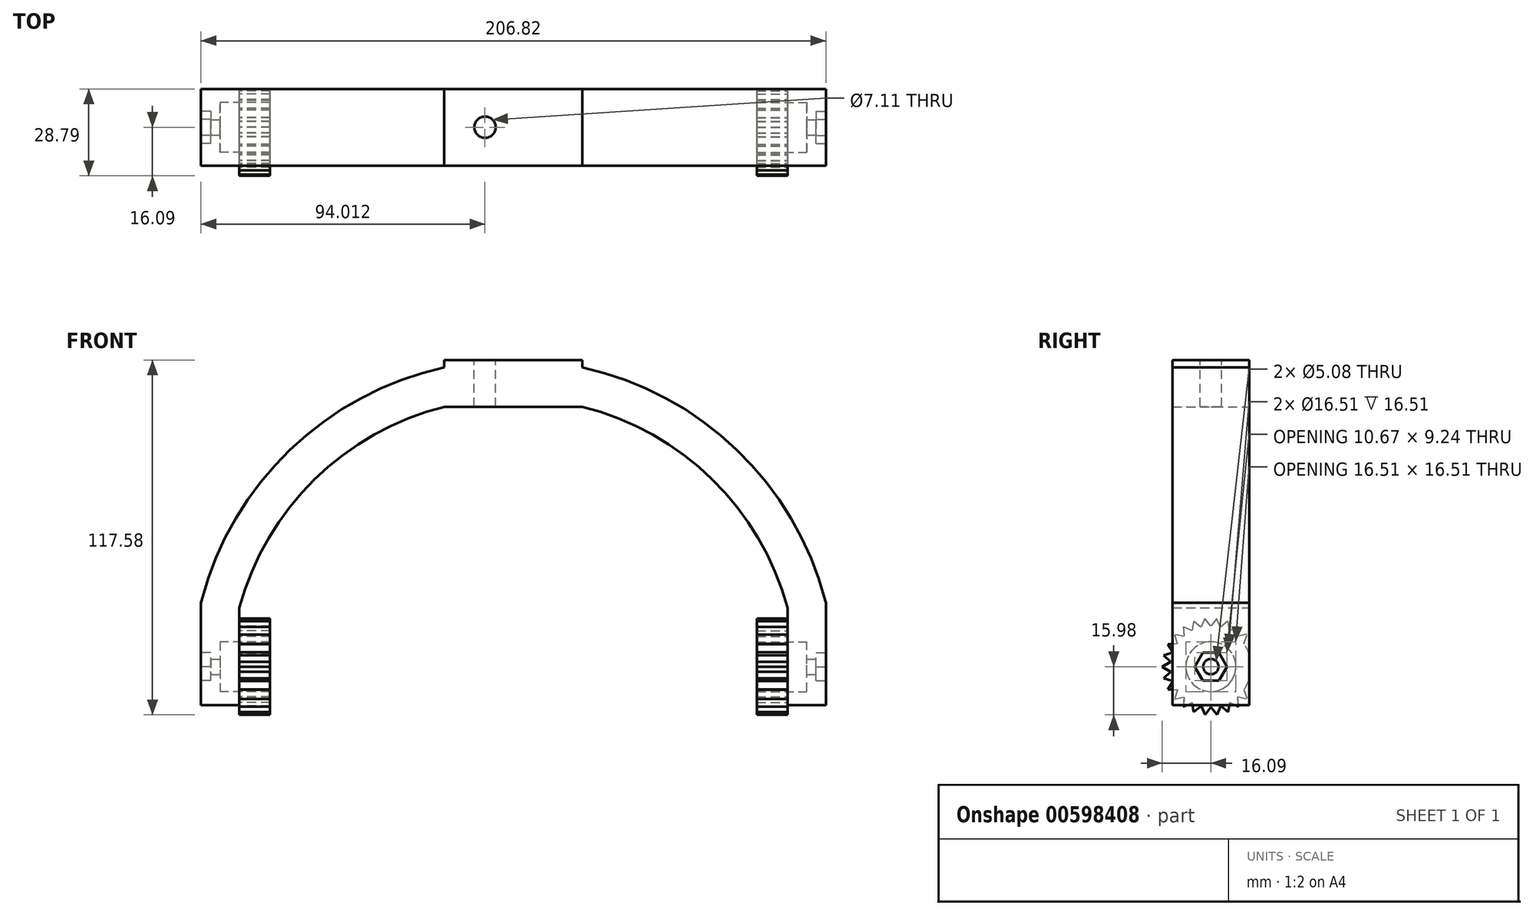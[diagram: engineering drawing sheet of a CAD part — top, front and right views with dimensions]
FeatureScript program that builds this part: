
annotation { "Feature Type Name" : "Feature", "Feature Type Description" : "" }
export const myFeature = defineFeature(function(context is Context, id is Id, definition is map)
    precondition{}
    {
        {
            var Q0;
            Q0=qCreatedBy(makeId("Front.planeOp"),FACE);
            var sketch = newSketch(context, id + "F0", { "sketchPlane" : qUnion([Q0])});
            skArc(sketch, "E0", {"start": v(97.06, 33.02) * mm, "mid": v(0, 107.95) * mm, "end": v(-97.06, 33.02) * mm});
            skLineSegment(sketch, "E1", {"start": v(-97.06, 33.02) * mm, "end": v(-97.06, 0) * mm});
            skLineSegment(sketch, "E2", {"start": v(97.06, 33.02) * mm, "end": v(97.06, 0) * mm});
            skSolve(sketch);
        }
        {
            var Q0;
            Q0=qCreatedBy(makeId("Top.planeOp"),FACE);
            var sketch = newSketch(context, id + "F1", { "sketchPlane" : qUnion([Q0])});
            skPoint(sketch, "E3.0", {"position": v(-97.06, 0) * mm});
            skLineSegment(sketch, "E4.bottom", {"start": v(-103.41, 12.7) * mm, "end": v(-90.71, 12.7) * mm});
            skLineSegment(sketch, "E4.top", {"start": v(-103.41, -12.7) * mm, "end": v(-90.71, -12.7) * mm});
            skLineSegment(sketch, "E4.left", {"start": v(-103.41, 12.7) * mm, "end": v(-103.41, -12.7) * mm});
            skLineSegment(sketch, "E4.right", {"start": v(-90.71, 12.7) * mm, "end": v(-90.71, -12.7) * mm});
            skSolve(sketch);
        }
        {
            var Q0;
            Q0 = qSketchRegion(id + "F1", true);
            var Q1;
            Q1 = qConstructionFilter(qBodyType(qCreatedBy(id + "F0" ,EDGE), BodyType.WIRE), ConstructionObject.NO);
            sweep(context, id + "F2", {"profiles" : qUnion([Q0]), "path" : qUnion([Q1])});
        }
        {
            var Q0;
            Q0=qCreatedBy(makeId("Right.planeOp"),FACE);
            var sketch = newSketch(context, id + "F3", { "sketchPlane" : qUnion([Q0])});
            skCircle(sketch, "E5", {"center": v(0, 12.7) * mm, "radius": 2.54 * mm});
            skSolve(sketch);
        }
        {
            var Q0;
            Q0 = qSketchRegion(id + "F3", true);
            extrude(context, id + "F4", {"entities" : qUnion([Q0]), "operationType" : NewBodyOperationType.REMOVE, "endBound" : BoundingType.SYMMETRIC, "oppositeDirection" : true, "depth" : 254 * mm, "offsetDistance" : 25.4 * mm});
        }
        {
            var Q0;
            Q0=makeQuery(id+"F2.opSweep","SWEPT_FACE",FACE,{"disambiguationData":[OSD([sQuery(id+"F0.wireOp",EDGE,"E2"),sQuery(id+"F1.wireOp",EDGE,"E4.left")])]});
            var Q1;
            Q1=makeQuery(id+"F2.opSweep","CAP_VERTEX",VERTEX,{"disambiguationData":[OSD([sQuery(id+"F0.wireOp",EDGE,"E2"),sQuery(id+"F1.wireOp",EDGE,"E4.bottom"),sQuery(id+"F1.wireOp",EDGE,"E4.left")])],"isStart":false});
            cPlane(context, id + "F5", {"entities" : qUnion([Q0, Q1]), "cplaneType" : CPlaneType.PLANE_POINT, "offset" : 25.4 * mm, "width" : 152.4 * mm, "height" : 152.4 * mm});
        }
        {
            var Q0;
            Q0=qCreatedBy(id+"F5.planeOp",FACE);
            var sketch = newSketch(context, id + "F6", { "sketchPlane" : qUnion([Q0])});
            skCircle(sketch, "E6", {"center": v(0, 12.7) * mm, "radius": 5.33 * mm, "construction": true});
            skLineSegment(sketch, "E7.0", {"start": v(-2.67, 17.32) * mm, "end": v(2.67, 17.32) * mm});
            skLineSegment(sketch, "E7.1", {"start": v(2.67, 17.32) * mm, "end": v(5.33, 12.7) * mm});
            skLineSegment(sketch, "E7.2", {"start": v(5.33, 12.7) * mm, "end": v(2.67, 8.08) * mm});
            skLineSegment(sketch, "E7.3", {"start": v(2.67, 8.08) * mm, "end": v(-2.67, 8.08) * mm});
            skLineSegment(sketch, "E7.4", {"start": v(-2.67, 8.08) * mm, "end": v(-5.33, 12.7) * mm});
            skLineSegment(sketch, "E7.5", {"start": v(-5.33, 12.7) * mm, "end": v(-2.67, 17.32) * mm});
            skSolve(sketch);
        }
        {
            var Q0;
            Q0=makeQuery(id+"F6.imprint","IMPRINT",FACE,{"disambiguationData":[TD([[makeQuery(id+"F6.imprint","IMPRINT",EDGE,{"derivedFrom":sQuery(id+"F6.wireOp",EDGE,"E7.0")}),-1.0]])]});
            extrude(context, id + "F7", {"entities" : qUnion([Q0]), "operationType" : NewBodyOperationType.REMOVE, "oppositeDirection" : true, "depth" : 3.3 * mm, "offsetDistance" : 25.4 * mm});
        }
        {
            var Q0;
            Q0=makeQuery(id+"F2.opSweep","SWEPT_FACE",FACE,{"disambiguationData":[OSD([sQuery(id+"F0.wireOp",EDGE,"E1"),sQuery(id+"F1.wireOp",EDGE,"E4.left")])]});
            var Q1;
            Q1=makeQuery(id+"F2.opSweep","CAP_VERTEX",VERTEX,{"disambiguationData":[OSD([sQuery(id+"F0.wireOp",EDGE,"E1"),sQuery(id+"F1.wireOp",EDGE,"E4.bottom"),sQuery(id+"F1.wireOp",EDGE,"E4.left")])],"isStart":true});
            cPlane(context, id + "F8", {"entities" : qUnion([Q0, Q1]), "cplaneType" : CPlaneType.PLANE_POINT, "offset" : 25.4 * mm, "width" : 152.4 * mm, "height" : 152.4 * mm});
        }
        {
            var Q0;
            Q0=qCreatedBy(id+"F8.planeOp",FACE);
            var sketch = newSketch(context, id + "F9", { "sketchPlane" : qUnion([Q0])});
            skLineSegment(sketch, "E8", {"start": v(0, 0) * mm, "end": v(0, 12.7) * mm, "construction": true});
            skCircle(sketch, "E9", {"center": v(0, 12.7) * mm, "radius": 5.33 * mm, "construction": true});
            skLineSegment(sketch, "E10.0", {"start": v(-2.67, 17.32) * mm, "end": v(2.67, 17.32) * mm});
            skLineSegment(sketch, "E10.1", {"start": v(2.67, 17.32) * mm, "end": v(5.33, 12.7) * mm});
            skLineSegment(sketch, "E10.2", {"start": v(5.33, 12.7) * mm, "end": v(2.67, 8.08) * mm});
            skLineSegment(sketch, "E10.3", {"start": v(2.67, 8.08) * mm, "end": v(-2.67, 8.08) * mm});
            skLineSegment(sketch, "E10.4", {"start": v(-2.67, 8.08) * mm, "end": v(-5.33, 12.7) * mm});
            skLineSegment(sketch, "E10.5", {"start": v(-5.33, 12.7) * mm, "end": v(-2.67, 17.32) * mm});
            skSolve(sketch);
        }
        {
            var Q0;
            Q0=makeQuery(id+"F9.imprint","IMPRINT",FACE,{"disambiguationData":[TD([[makeQuery(id+"F9.imprint","IMPRINT",EDGE,{"derivedFrom":sQuery(id+"F9.wireOp",EDGE,"E10.0")}),-1.0]])]});
            extrude(context, id + "F10", {"entities" : qUnion([Q0]), "operationType" : NewBodyOperationType.REMOVE, "oppositeDirection" : true, "depth" : 3.3 * mm, "offsetDistance" : 25.4 * mm});
        }
        {
            var Q0;
            Q0=makeQuery(id+"F2.opSweep","SWEPT_FACE",FACE,{"disambiguationData":[OSD([sQuery(id+"F0.wireOp",EDGE,"E1"),sQuery(id+"F1.wireOp",EDGE,"E4.left")])]});
            cPlane(context, id + "F11", {"entities" : qUnion([Q0]), "cplaneType" : CPlaneType.OFFSET, "offset" : 6.35 * mm, "oppositeDirection" : true, "width" : 152.4 * mm, "height" : 152.4 * mm});
        }
        {
            var Q0;
            Q0=qCreatedBy(id+"F11.planeOp",FACE);
            var sketch = newSketch(context, id + "F12", { "sketchPlane" : qUnion([Q0])});
            skLineSegment(sketch, "E11", {"start": v(0, 0) * mm, "end": v(0, 12.7) * mm, "construction": true});
            skCircle(sketch, "E12", {"center": v(0, 12.7) * mm, "radius": 8.26 * mm});
            skSolve(sketch);
        }
        {
            var Q0;
            Q0=makeQuery(id+"F2.opSweep","SWEPT_FACE",FACE,{"disambiguationData":[OSD([sQuery(id+"F0.wireOp",EDGE,"E2"),sQuery(id+"F1.wireOp",EDGE,"E4.left")])]});
            cPlane(context, id + "F13", {"entities" : qUnion([Q0]), "cplaneType" : CPlaneType.OFFSET, "offset" : 6.35 * mm, "oppositeDirection" : true, "width" : 152.4 * mm, "height" : 152.4 * mm});
        }
        {
            var Q0;
            Q0=qCreatedBy(id+"F13.planeOp",FACE);
            var sketch = newSketch(context, id + "F14", { "sketchPlane" : qUnion([Q0])});
            skLineSegment(sketch, "E13", {"start": v(0, 0) * mm, "end": v(0, 12.7) * mm, "construction": true});
            skCircle(sketch, "E14", {"center": v(0, 12.7) * mm, "radius": 8.26 * mm});
            skSolve(sketch);
        }
        {
            var Q0;
            Q0=makeQuery(id+"F2.opSweep","SWEPT_FACE",FACE,{"disambiguationData":[OSD([sQuery(id+"F0.wireOp",EDGE,"E1"),sQuery(id+"F1.wireOp",EDGE,"E4.right")])]});
            var sketch = newSketch(context, id + "F15", { "sketchPlane" : qUnion([Q0])});
            skLineSegment(sketch, "E15", {"start": v(0, 0) * mm, "end": v(0, 12.7) * mm, "construction": true});
            skLineSegment(sketch, "E16", {"start": v(0, 12.7) * mm, "end": v(0, 26.04) * mm, "construction": true});
            skLineSegment(sketch, "E17", {"start": v(0, 26.04) * mm, "end": v(-2, 28.67) * mm});
            skLineSegment(sketch, "E18", {"start": v(-2, 28.67) * mm, "end": v(-3.28, 25.63) * mm});
            skLineSegment(sketch, "E19.1.0", {"start": v(-3.2, 25.65) * mm, "end": v(-5.76, 27.73) * mm});
            skLineSegment(sketch, "E19.1.1", {"start": v(-5.76, 27.73) * mm, "end": v(-6.27, 24.47) * mm});
            skLineSegment(sketch, "E19.2.0", {"start": v(-6.2, 24.5) * mm, "end": v(-9.18, 25.91) * mm});
            skLineSegment(sketch, "E19.2.1", {"start": v(-9.18, 25.91) * mm, "end": v(-8.9, 22.62) * mm});
            skLineSegment(sketch, "E19.3.0", {"start": v(-8.84, 22.68) * mm, "end": v(-12.08, 23.33) * mm});
            skLineSegment(sketch, "E19.3.1", {"start": v(-12.08, 23.33) * mm, "end": v(-11.02, 20.2) * mm});
            skLineSegment(sketch, "E19.4.0", {"start": v(-10.97, 20.28) * mm, "end": v(-14.27, 20.13) * mm});
            skLineSegment(sketch, "E19.4.1", {"start": v(-14.27, 20.13) * mm, "end": v(-12.5, 17.35) * mm});
            skLineSegment(sketch, "E19.5.0", {"start": v(-12.47, 17.43) * mm, "end": v(-15.64, 16.5) * mm});
            skLineSegment(sketch, "E19.5.1", {"start": v(-15.64, 16.5) * mm, "end": v(-13.25, 14.22) * mm});
            skLineSegment(sketch, "E19.6.0", {"start": v(-13.24, 14.3) * mm, "end": v(-16.1, 12.65) * mm});
            skLineSegment(sketch, "E19.6.1", {"start": v(-16.1, 12.65) * mm, "end": v(-13.23, 11) * mm});
            skLineSegment(sketch, "E19.7.0", {"start": v(-13.24, 11.1) * mm, "end": v(-15.61, 8.8) * mm});
            skLineSegment(sketch, "E19.7.1", {"start": v(-15.61, 8.8) * mm, "end": v(-12.44, 7.89) * mm});
            skLineSegment(sketch, "E19.8.0", {"start": v(-12.47, 7.97) * mm, "end": v(-14.22, 5.17) * mm});
            skLineSegment(sketch, "E19.8.1", {"start": v(-14.22, 5.17) * mm, "end": v(-10.92, 5.05) * mm});
            skLineSegment(sketch, "E19.9.0", {"start": v(-10.97, 5.12) * mm, "end": v(-12, 1.99) * mm});
            skLineSegment(sketch, "E19.9.1", {"start": v(-12, 1.99) * mm, "end": v(-8.78, 2.66) * mm});
            skLineSegment(sketch, "E19.10.0", {"start": v(-8.84, 2.72) * mm, "end": v(-9.1, -0.57) * mm});
            skLineSegment(sketch, "E19.10.1", {"start": v(-9.1, -0.57) * mm, "end": v(-6.12, 0.85) * mm});
            skLineSegment(sketch, "E19.11.0", {"start": v(-6.2, 0.9) * mm, "end": v(-5.66, -2.37) * mm});
            skLineSegment(sketch, "E19.11.1", {"start": v(-5.66, -2.37) * mm, "end": v(-3.1, -0.27) * mm});
            skLineSegment(sketch, "E19.12.0", {"start": v(-3.2, -0.25) * mm, "end": v(-1.89, -3.28) * mm});
            skLineSegment(sketch, "E19.12.1", {"start": v(-1.89, -3.28) * mm, "end": v(0.09, -0.63) * mm});
            skLineSegment(sketch, "E19.13.0", {"start": v(0, -0.63) * mm, "end": v(2, -3.27) * mm});
            skLineSegment(sketch, "E19.13.1", {"start": v(2, -3.27) * mm, "end": v(3.28, -0.23) * mm});
            skLineSegment(sketch, "E19.14.0", {"start": v(3.2, -0.25) * mm, "end": v(5.76, -2.33) * mm});
            skLineSegment(sketch, "E19.14.1", {"start": v(5.76, -2.33) * mm, "end": v(6.27, 0.93) * mm});
            skLineSegment(sketch, "E19.15.0", {"start": v(6.2, 0.9) * mm, "end": v(9.18, -0.51) * mm});
            skLineSegment(sketch, "E19.15.1", {"start": v(9.18, -0.51) * mm, "end": v(8.9, 2.78) * mm});
            skLineSegment(sketch, "E19.16.0", {"start": v(8.84, 2.72) * mm, "end": v(12.08, 2.07) * mm});
            skLineSegment(sketch, "E19.16.1", {"start": v(12.08, 2.07) * mm, "end": v(11.02, 5.2) * mm});
            skLineSegment(sketch, "E19.17.0", {"start": v(10.97, 5.12) * mm, "end": v(11.05, 5.13) * mm});
            skLineSegment(sketch, "E19.21.1", {"start": v(11, 20.34) * mm, "end": v(10.92, 20.35) * mm});
            skLineSegment(sketch, "E19.22.0", {"start": v(10.97, 20.28) * mm, "end": v(12, 23.41) * mm});
            skLineSegment(sketch, "E19.22.1", {"start": v(12, 23.41) * mm, "end": v(8.78, 22.74) * mm});
            skLineSegment(sketch, "E19.23.0", {"start": v(8.84, 22.68) * mm, "end": v(9.1, 25.97) * mm});
            skLineSegment(sketch, "E19.23.1", {"start": v(9.1, 25.97) * mm, "end": v(6.12, 24.55) * mm});
            skLineSegment(sketch, "E19.24.0", {"start": v(6.2, 24.5) * mm, "end": v(5.66, 27.77) * mm});
            skLineSegment(sketch, "E19.24.1", {"start": v(5.66, 27.77) * mm, "end": v(3.1, 25.67) * mm});
            skLineSegment(sketch, "E19.25.0", {"start": v(3.2, 25.65) * mm, "end": v(1.89, 28.68) * mm});
            skLineSegment(sketch, "E19.25.1", {"start": v(1.89, 28.68) * mm, "end": v(-0.09, 26.03) * mm});
            skPoint(sketch, "E19.center", {"position": v(0, 12.7) * mm});
            skLineSegment(sketch, "E20", {"start": v(12.7, 16.77) * mm, "end": v(12.7, 8.63) * mm});
            skArc(sketch, "E21", {"start": v(8.84, 22.68) * mm, "mid": v(8.8, 22.71) * mm, "end": v(8.78, 22.74) * mm});
            skArc(sketch, "E22.trimOffspring", {"start": v(6.2, 24.5) * mm, "mid": v(6.16, 24.53) * mm, "end": v(6.12, 24.55) * mm});
            skArc(sketch, "E23.trimOffspring", {"start": v(3.2, 25.65) * mm, "mid": v(3.15, 25.66) * mm, "end": v(3.1, 25.67) * mm});
            skArc(sketch, "E24.trimOffspring", {"start": v(0, 26.03) * mm, "mid": v(-0.04, 26.03) * mm, "end": v(-0.09, 26.03) * mm});
            skArc(sketch, "E25.trimOffspring", {"start": v(-3.2, 25.65) * mm, "mid": v(-3.23, 25.64) * mm, "end": v(-3.28, 25.63) * mm});
            skArc(sketch, "E26.trimOffspring", {"start": v(-6.2, 24.5) * mm, "mid": v(-6.24, 24.49) * mm, "end": v(-6.27, 24.47) * mm});
            skArc(sketch, "E27.trimOffspring", {"start": v(-8.84, 22.68) * mm, "mid": v(-8.88, 22.65) * mm, "end": v(-8.9, 22.62) * mm});
            skArc(sketch, "E28.trimOffspring", {"start": v(-10.97, 20.28) * mm, "mid": v(-11, 20.24) * mm, "end": v(-11.02, 20.2) * mm});
            skArc(sketch, "E29.trimOffspring", {"start": v(-12.47, 17.43) * mm, "mid": v(-12.48, 17.39) * mm, "end": v(-12.5, 17.35) * mm});
            skArc(sketch, "E30.trimOffspring", {"start": v(-13.24, 14.3) * mm, "mid": v(-13.24, 14.26) * mm, "end": v(-13.25, 14.22) * mm});
            skArc(sketch, "E31.trimOffspring", {"start": v(-13.24, 11.1) * mm, "mid": v(-13.23, 11.05) * mm, "end": v(-13.23, 11) * mm});
            skArc(sketch, "E32.trimOffspring", {"start": v(-12.47, 7.97) * mm, "mid": v(-12.45, 7.93) * mm, "end": v(-12.44, 7.89) * mm});
            skArc(sketch, "E33.trimOffspring", {"start": v(-10.97, 5.12) * mm, "mid": v(-10.95, 5.09) * mm, "end": v(-10.92, 5.05) * mm});
            skArc(sketch, "E34.trimOffspring", {"start": v(-6.2, 0.9) * mm, "mid": v(-6.16, 0.87) * mm, "end": v(-6.12, 0.85) * mm});
            skArc(sketch, "E35.trimOffspring", {"start": v(0, -0.63) * mm, "mid": v(0.04, -0.63) * mm, "end": v(0.09, -0.63) * mm});
            skArc(sketch, "E36.trimOffspring", {"start": v(-3.2, -0.25) * mm, "mid": v(-3.15, -0.26) * mm, "end": v(-3.1, -0.27) * mm});
            skArc(sketch, "E37.trimOffspring", {"start": v(6.2, 0.9) * mm, "mid": v(6.24, 0.91) * mm, "end": v(6.27, 0.93) * mm});
            skArc(sketch, "E38.trimOffspring", {"start": v(10.97, 5.12) * mm, "mid": v(11.97, 6.82) * mm, "end": v(12.7, 8.63) * mm});
            skArc(sketch, "E39.trimOffspring", {"start": v(8.84, 2.72) * mm, "mid": v(8.88, 2.75) * mm, "end": v(8.9, 2.78) * mm});
            skArc(sketch, "E40.trimOffspring", {"start": v(12.7, 16.77) * mm, "mid": v(11.95, 18.62) * mm, "end": v(10.92, 20.35) * mm});
            skSolve(sketch);
        }
        {
            var Q0;
            Q0 = qSketchRegion(id + "F15", true);
            extrude(context, id + "F16", {"entities" : qUnion([Q0]), "operationType" : NewBodyOperationType.ADD, "depth" : 10.16 * mm, "offsetDistance" : 25.4 * mm});
        }
        {
            var Q0;
            Q0=makeQuery(id+"F2.opSweep","SWEPT_FACE",FACE,{"disambiguationData":[OSD([sQuery(id+"F0.wireOp",EDGE,"E2"),sQuery(id+"F1.wireOp",EDGE,"E4.right")])]});
            var sketch = newSketch(context, id + "F17", { "sketchPlane" : qUnion([Q0])});
            skLineSegment(sketch, "E41", {"start": v(0, 0) * mm, "end": v(0, 12.7) * mm, "construction": true});
            skArc(sketch, "E42.MirrorCS", {"start": v(0, 26.03) * mm, "mid": v(0.04, 26.03) * mm, "end": v(0.09, 26.03) * mm});
            skLineSegment(sketch, "E43.MirrorCS", {"start": v(-11, 20.34) * mm, "end": v(-10.92, 20.35) * mm});
            skArc(sketch, "E44.MirrorCS", {"start": v(8.84, 22.68) * mm, "mid": v(8.88, 22.65) * mm, "end": v(8.9, 22.62) * mm});
            skArc(sketch, "E45.MirrorCS", {"start": v(10.97, 5.12) * mm, "mid": v(10.95, 5.09) * mm, "end": v(10.92, 5.05) * mm});
            skLineSegment(sketch, "E46.MirrorCS", {"start": v(-10.97, 5.12) * mm, "end": v(-11.05, 5.13) * mm});
            skArc(sketch, "E47.MirrorCS", {"start": v(6.2, 24.5) * mm, "mid": v(6.24, 24.49) * mm, "end": v(6.27, 24.47) * mm});
            skArc(sketch, "E48.MirrorCS", {"start": v(0, -0.63) * mm, "mid": v(-0.04, -0.63) * mm, "end": v(-0.09, -0.63) * mm});
            skArc(sketch, "E49.MirrorCS", {"start": v(12.47, 7.97) * mm, "mid": v(12.45, 7.93) * mm, "end": v(12.44, 7.89) * mm});
            skArc(sketch, "E50.MirrorCS", {"start": v(3.2, 25.65) * mm, "mid": v(3.23, 25.64) * mm, "end": v(3.28, 25.63) * mm});
            skArc(sketch, "E51.MirrorCS", {"start": v(6.2, 0.9) * mm, "mid": v(6.16, 0.87) * mm, "end": v(6.12, 0.85) * mm});
            skArc(sketch, "E52.MirrorCS", {"start": v(13.24, 11.1) * mm, "mid": v(13.23, 11.05) * mm, "end": v(13.23, 11) * mm});
            skArc(sketch, "E53.MirrorCS", {"start": v(-3.2, 25.65) * mm, "mid": v(-3.15, 25.66) * mm, "end": v(-3.1, 25.67) * mm});
            skArc(sketch, "E54.MirrorCS", {"start": v(-8.84, 2.72) * mm, "mid": v(-8.88, 2.75) * mm, "end": v(-8.9, 2.78) * mm});
            skArc(sketch, "E55.MirrorCS", {"start": v(12.47, 17.43) * mm, "mid": v(12.48, 17.39) * mm, "end": v(12.5, 17.35) * mm});
            skArc(sketch, "E56.MirrorCS", {"start": v(-6.2, 24.5) * mm, "mid": v(-6.16, 24.53) * mm, "end": v(-6.12, 24.55) * mm});
            skArc(sketch, "E57.MirrorCS", {"start": v(-8.84, 22.68) * mm, "mid": v(-8.8, 22.71) * mm, "end": v(-8.78, 22.74) * mm});
            skArc(sketch, "E58.MirrorCS", {"start": v(-6.2, 0.9) * mm, "mid": v(-6.24, 0.91) * mm, "end": v(-6.27, 0.93) * mm});
            skArc(sketch, "E59.MirrorCS", {"start": v(10.97, 20.28) * mm, "mid": v(11, 20.24) * mm, "end": v(11.02, 20.2) * mm});
            skArc(sketch, "E60.MirrorCS", {"start": v(13.24, 14.3) * mm, "mid": v(13.24, 14.26) * mm, "end": v(13.25, 14.22) * mm});
            skLineSegment(sketch, "E61.MirrorCS", {"start": v(-3.2, -0.25) * mm, "end": v(-5.76, -2.33) * mm});
            skArc(sketch, "E62.MirrorCS", {"start": v(3.2, -0.25) * mm, "mid": v(3.15, -0.26) * mm, "end": v(3.1, -0.27) * mm});
            skLineSegment(sketch, "E63.MirrorCS", {"start": v(1.89, -3.28) * mm, "end": v(-0.09, -0.63) * mm});
            skLineSegment(sketch, "E64.MirrorCS", {"start": v(-5.66, 27.77) * mm, "end": v(-3.1, 25.67) * mm});
            skLineSegment(sketch, "E65.MirrorCS", {"start": v(14.27, 20.13) * mm, "end": v(12.5, 17.35) * mm});
            skLineSegment(sketch, "E66.MirrorCS", {"start": v(8.84, 22.68) * mm, "end": v(12.08, 23.33) * mm});
            skLineSegment(sketch, "E67.MirrorCS", {"start": v(6.2, 24.5) * mm, "end": v(9.18, 25.91) * mm});
            skLineSegment(sketch, "E68.MirrorCS", {"start": v(3.2, 25.65) * mm, "end": v(5.76, 27.73) * mm});
            skLineSegment(sketch, "E69.MirrorCS", {"start": v(2, 28.67) * mm, "end": v(3.28, 25.63) * mm});
            skLineSegment(sketch, "E70.MirrorCS", {"start": v(0, 26.04) * mm, "end": v(2, 28.67) * mm});
            skLineSegment(sketch, "E71.MirrorCS", {"start": v(13.24, 14.3) * mm, "end": v(16.1, 12.65) * mm});
            skLineSegment(sketch, "E72.MirrorCS", {"start": v(-2, -3.27) * mm, "end": v(-3.28, -0.23) * mm});
            skLineSegment(sketch, "E73.MirrorCS", {"start": v(-1.89, 28.68) * mm, "end": v(0.09, 26.03) * mm});
            skLineSegment(sketch, "E74.MirrorCS", {"start": v(15.64, 16.5) * mm, "end": v(13.25, 14.22) * mm});
            skLineSegment(sketch, "E75.MirrorCS", {"start": v(10.97, 5.12) * mm, "end": v(12, 1.99) * mm});
            skLineSegment(sketch, "E76.MirrorCS", {"start": v(3.2, -0.25) * mm, "end": v(1.89, -3.28) * mm});
            skLineSegment(sketch, "E77.MirrorCS", {"start": v(0, -0.63) * mm, "end": v(-2, -3.27) * mm});
            skLineSegment(sketch, "E78.MirrorCS", {"start": v(-12.08, 2.07) * mm, "end": v(-11.02, 5.2) * mm});
            skLineSegment(sketch, "E79.MirrorCS", {"start": v(-3.2, 25.65) * mm, "end": v(-1.89, 28.68) * mm});
            skLineSegment(sketch, "E80.MirrorCS", {"start": v(5.66, -2.37) * mm, "end": v(3.1, -0.27) * mm});
            skLineSegment(sketch, "E81.MirrorCS", {"start": v(-9.1, 25.97) * mm, "end": v(-6.12, 24.55) * mm});
            skLineSegment(sketch, "E82.MirrorCS", {"start": v(12.47, 7.97) * mm, "end": v(14.22, 5.17) * mm});
            skLineSegment(sketch, "E83.MirrorCS", {"start": v(6.2, 0.9) * mm, "end": v(5.66, -2.37) * mm});
            skLineSegment(sketch, "E84.MirrorCS", {"start": v(9.1, -0.57) * mm, "end": v(6.12, 0.85) * mm});
            skLineSegment(sketch, "E85.MirrorCS", {"start": v(13.24, 11.1) * mm, "end": v(15.61, 8.8) * mm});
            skLineSegment(sketch, "E86.MirrorCS", {"start": v(-5.76, -2.33) * mm, "end": v(-6.27, 0.93) * mm});
            skLineSegment(sketch, "E87.MirrorCS", {"start": v(16.1, 12.65) * mm, "end": v(13.23, 11) * mm});
            skLineSegment(sketch, "E88.MirrorCS", {"start": v(12, 1.99) * mm, "end": v(8.78, 2.66) * mm});
            skLineSegment(sketch, "E89.MirrorCS", {"start": v(5.76, 27.73) * mm, "end": v(6.27, 24.47) * mm});
            skLineSegment(sketch, "E90.MirrorCS", {"start": v(-12.7, 16.77) * mm, "end": v(-12.7, 8.63) * mm});
            skLineSegment(sketch, "E91.MirrorCS", {"start": v(10.97, 20.28) * mm, "end": v(14.27, 20.13) * mm});
            skLineSegment(sketch, "E92.MirrorCS", {"start": v(12.08, 23.33) * mm, "end": v(11.02, 20.2) * mm});
            skLineSegment(sketch, "E93.MirrorCS", {"start": v(9.18, 25.91) * mm, "end": v(8.9, 22.62) * mm});
            skLineSegment(sketch, "E94.MirrorCS", {"start": v(0, 12.7) * mm, "end": v(0, 26.04) * mm, "construction": true});
            skLineSegment(sketch, "E95.MirrorCS", {"start": v(12.47, 17.43) * mm, "end": v(15.64, 16.5) * mm});
            skLineSegment(sketch, "E96.MirrorCS", {"start": v(-6.2, 24.5) * mm, "end": v(-5.66, 27.77) * mm});
            skLineSegment(sketch, "E97.MirrorCS", {"start": v(14.22, 5.17) * mm, "end": v(10.92, 5.05) * mm});
            skLineSegment(sketch, "E98.MirrorCS", {"start": v(-8.84, 2.72) * mm, "end": v(-12.08, 2.07) * mm});
            skArc(sketch, "E99.MirrorCS", {"start": v(-12.7, 16.77) * mm, "mid": v(-11.95, 18.62) * mm, "end": v(-10.92, 20.35) * mm});
            skLineSegment(sketch, "E100.MirrorCS", {"start": v(-8.84, 22.68) * mm, "end": v(-9.1, 25.97) * mm});
            skLineSegment(sketch, "E101.MirrorCS", {"start": v(-9.18, -0.51) * mm, "end": v(-8.9, 2.78) * mm});
            skLineSegment(sketch, "E102.MirrorCS", {"start": v(15.61, 8.8) * mm, "end": v(12.44, 7.89) * mm});
            skLineSegment(sketch, "E103.MirrorCS", {"start": v(-12, 23.41) * mm, "end": v(-8.78, 22.74) * mm});
            skLineSegment(sketch, "E104.MirrorCS", {"start": v(-6.2, 0.9) * mm, "end": v(-9.18, -0.51) * mm});
            skArc(sketch, "E105.MirrorCS", {"start": v(-10.97, 5.12) * mm, "mid": v(-11.97, 6.82) * mm, "end": v(-12.7, 8.63) * mm});
            skLineSegment(sketch, "E106.MirrorCS", {"start": v(8.84, 2.72) * mm, "end": v(9.1, -0.57) * mm});
            skLineSegment(sketch, "E107.MirrorCS", {"start": v(-10.97, 20.28) * mm, "end": v(-12, 23.41) * mm});
            skSolve(sketch);
        }
        {
            var Q0;
            Q0 = qSketchRegion(id + "F17", true);
            var Q1;
            Q1=makeQuery(id+"F2.opSweep","SWEPT_FACE",FACE,{"disambiguationData":[OSD([sQuery(id+"F0.wireOp",EDGE,"E2"),sQuery(id+"F1.wireOp",EDGE,"E4.left")])]});
            extrude(context, id + "F18", {"entities" : qUnion([Q0, Q1]), "operationType" : NewBodyOperationType.ADD, "depth" : 10.16 * mm, "offsetDistance" : 25.4 * mm});
        }
        {
            var Q0;
            Q0 = qSketchRegion(id + "F12", true);
            extrude(context, id + "F19", {"entities" : qUnion([Q0]), "operationType" : NewBodyOperationType.REMOVE, "oppositeDirection" : true, "depth" : 63.75 * mm, "offsetDistance" : 25.4 * mm});
        }
        {
            var Q0;
            Q0 = qSketchRegion(id + "F14", true);
            extrude(context, id + "F20", {"entities" : qUnion([Q0]), "operationType" : NewBodyOperationType.REMOVE, "oppositeDirection" : true, "depth" : 25.4 * mm, "offsetDistance" : 25.4 * mm});
        }
        {
            var Q0;
            Q0=makeQuery(id+"F2.opSweep","SWEPT_EDGE",EDGE,{"disambiguationData":[OSD([sQuery(id+"F0.wireOp",EDGE,"E0"),sQuery(id+"F1.wireOp",EDGE,"E4.top"),sQuery(id+"F1.wireOp",EDGE,"E4.left")]),OD(2.0)]});
            cPoint(context, id + "F21", {"entities" : qUnion([Q0]), "parameter" : 0.5});
        }
        {
            var Q0;
            Q0=qCreatedBy(makeId("Top.planeOp"),FACE);
            var Q1;
            Q1 = qCreatedBy(id + "F21" ,VERTEX);
            cPlane(context, id + "F22", {"entities" : qUnion([Q0, Q1]), "cplaneType" : CPlaneType.PLANE_POINT, "offset" : 25.4 * mm, "width" : 152.4 * mm, "height" : 152.4 * mm});
        }
        {
            var Q0;
            Q0=qCreatedBy(id+"F22.planeOp",FACE);
            var sketch = newSketch(context, id + "F23", { "sketchPlane" : qUnion([Q0])});
            skFitSpline(sketch, "E108.0", {"points": [v(-103.2, 12.7) * mm, v(-34.4, 12.7) * mm, v(34.4, 12.7) * mm, v(103.2, 12.7) * mm]});
            skLineSegment(sketch, "E109.bottom", {"start": v(-22.86, 12.7) * mm, "end": v(22.86, 12.7) * mm});
            skLineSegment(sketch, "E109.top", {"start": v(-22.86, -12.7) * mm, "end": v(22.86, -12.7) * mm});
            skLineSegment(sketch, "E109.left", {"start": v(-22.86, 12.7) * mm, "end": v(-22.86, -12.7) * mm});
            skLineSegment(sketch, "E109.right", {"start": v(22.86, 12.7) * mm, "end": v(22.86, -12.7) * mm});
            skPoint(sketch, "E109.middle", {"position": v(0, 0) * mm});
            skSolve(sketch);
        }
        {
            var Q0;
            Q0 = qSketchRegion(id + "F23", true);
            extrude(context, id + "F24", {"entities" : qUnion([Q0]), "operationType" : NewBodyOperationType.ADD, "oppositeDirection" : true, "depth" : 15.5 * mm, "offsetDistance" : 25.4 * mm});
        }
        {
            var Q0;
            Q0=qCreatedBy(id+"F22.planeOp",FACE);
            var sketch = newSketch(context, id + "F25", { "sketchPlane" : qUnion([Q0])});
            skCircle(sketch, "E110", {"center": v(-9.4, 0) * mm, "radius": 3.56 * mm});
            skCircle(sketch, "E111.MirrorC", {"center": v(9.4, 0) * mm, "radius": 3.56 * mm});
            skSolve(sketch);
        }
        {
            var Q0;
            Q0=makeQuery(id+"F25.imprint","IMPRINT",FACE,{"disambiguationData":[TD([[makeQuery(id+"F25.imprint","IMPRINT",EDGE,{"derivedFrom":sQuery(id+"F25.wireOp",EDGE,"E110")}),1.0]])]});
            var Q1;
            Q1=makeQuery(id+"F25.imprint","IMPRINT",FACE,{"disambiguationData":[TD([[makeQuery(id+"F25.imprint","IMPRINT",EDGE,{"derivedFrom":sQuery(id+"F25.wireOp",EDGE,"E111.MirrorC")}),-1.0]])]});
            extrude(context, id + "F26", {"entities" : qUnion([Q0, Q1]), "operationType" : NewBodyOperationType.REMOVE, "oppositeDirection" : true, "depth" : 25.4 * mm, "offsetDistance" : 25.4 * mm});
        }
    });
